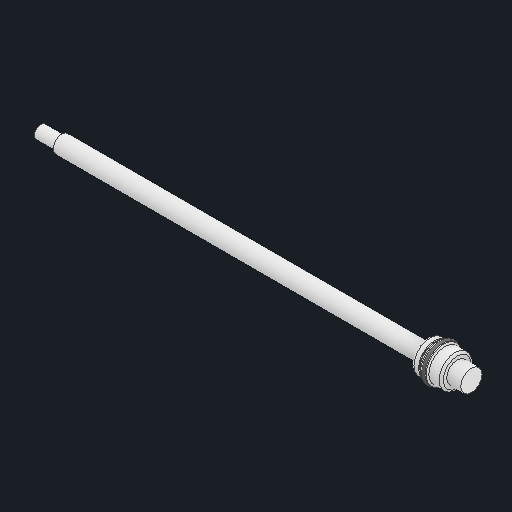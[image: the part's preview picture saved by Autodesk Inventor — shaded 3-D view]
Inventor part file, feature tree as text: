
AUTODESK INVENTOR PART (.ipt)
format: ipt  version: 2023 (Build 270158000, 158)  size: 144,896 bytes
history: native  units: in
note: dims shown in document units (in); Inventor stores cm internally (conversion verified against a paired STEP export)
features: revolve x2
ambient origin geometry x8: Origin, YZ Plane, XZ Plane, XY Plane, X Axis, Y Axis, Z Axis, Center Point
bodies: Solid1 (feature_tree), Solid2 (feature_tree)
feature tree (2):
  revolve  "Revolve1"  [1 undecoded]
  revolve  "Revolve2"  [1 undecoded]
note: 2 required parameter values undecoded (feature->parameter linkage not recoverable at this tier; creation-order binding heuristic only, values carry confidence <= 0.55)
